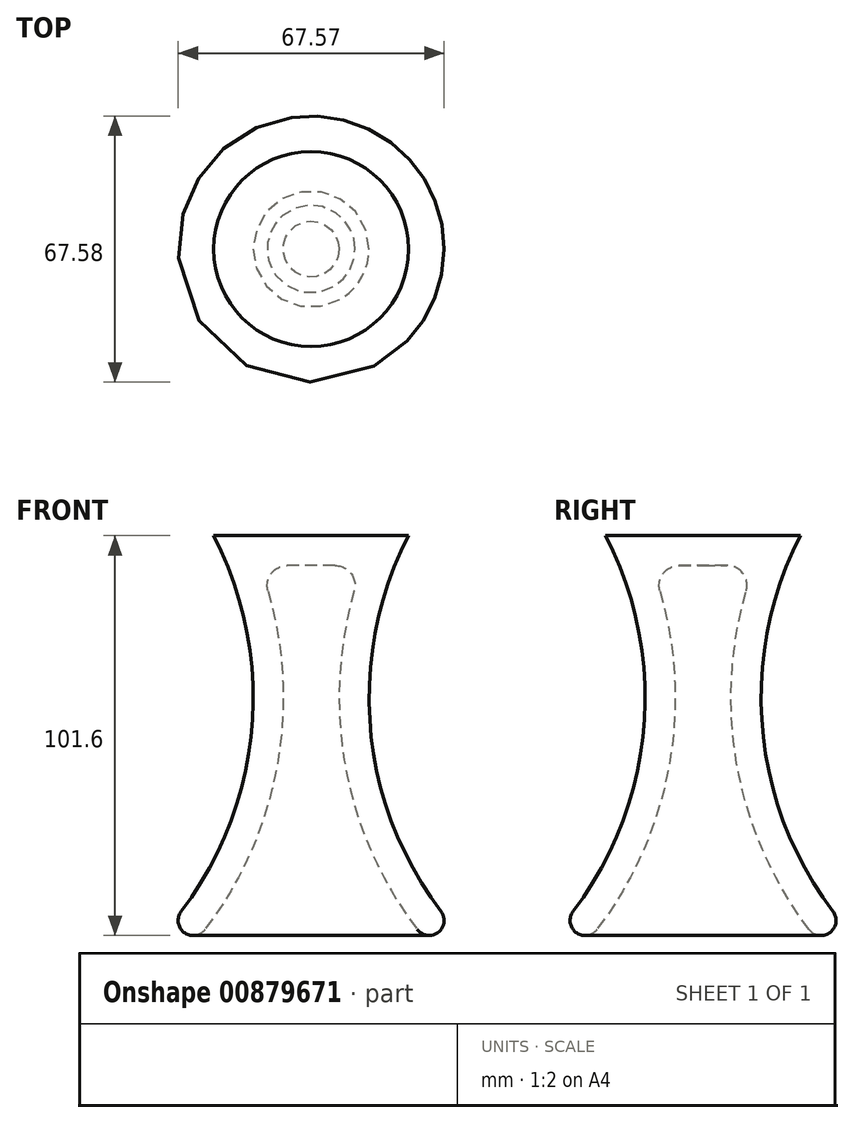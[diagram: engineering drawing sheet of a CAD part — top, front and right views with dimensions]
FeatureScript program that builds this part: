
annotation { "Feature Type Name" : "Feature", "Feature Type Description" : "" }
export const myFeature = defineFeature(function(context is Context, id is Id, definition is map)
    precondition{}
    {
        {
            var Q0;
            Q0=qCreatedBy(makeId("Front.planeOp"),FACE);
            var sketch = newSketch(context, id + "F0", { "sketchPlane" : qUnion([Q0])});
            skLineSegment(sketch, "E0", {"start": v(143.9, 51.31) * mm, "end": v(143.9, -50.29) * mm});
            skLineSegment(sketch, "E1", {"start": v(143.9, 51.31) * mm, "end": v(119.14, 51.31) * mm});
            skLineSegment(sketch, "E2", {"start": v(143.9, -50.29) * mm, "end": v(105.8, -50.29) * mm});
            skArc(sketch, "E3", {"start": v(105.8, -50.29) * mm, "mid": v(128.4, -1.58) * mm, "end": v(119.14, 51.31) * mm});
            skSolve(sketch);
        }
        {
            var Q0;
            Q0=makeQuery(id+"F0.imprint","IMPRINT",FACE,{"disambiguationData":[TD([[makeQuery(id+"F0.imprint","IMPRINT",EDGE,{"derivedFrom":sQuery(id+"F0.wireOp",EDGE,"E0")}),-1.0]])]});
            var Q1;
            Q1=sQuery(id+"F0.wireOp",EDGE,"E0");
            revolve(context, id + "F1", {"surfaceOperationType" : NewSurfaceOperationType.NEW, "entities" : qUnion([Q0]), "axis" : qUnion([Q1]), "revolveType" : RevolveType.FULL});
        }
        {
            var Q0;
            Q0=makeQuery(id+"F1.opRevolve","SWEPT_FACE",FACE,{"disambiguationData":[OSD([sQuery(id+"F0.wireOp",EDGE,"E2")])]});
            shell(context, id + "F2", {"entities" : qUnion([Q0]), "thickness" : 7.62 * mm});
        }
        {
            var Q0;
            Q0=makeQuery(id+"F2.opShell","OFFSET_EDGE",EDGE,{"disambiguationData":[OSD([sQuery(id+"F0.wireOp",EDGE,"E2"),sQuery(id+"F0.wireOp",EDGE,"E3")])]});
            var Q1;
            Q1=makeQuery(id+"F1.opRevolve","SWEPT_EDGE",EDGE,{"disambiguationData":[OSD([sQuery(id+"F0.wireOp",EDGE,"E2"),sQuery(id+"F0.wireOp",EDGE,"E3")])]});
            fillet(context, id + "F3", {"entities" : qUnion([Q0, Q1]), "radius" : 3.8 * mm, "tangentPropagation" : true, "allowEdgeOverflow" : false});
        }
        {
            var Q0;
            Q0=makeQuery(id+"F2.opShell","OFFSET_FACE",FACE,{"disambiguationData":[OSD([sQuery(id+"F0.wireOp",EDGE,"E1")])]});
            fillet(context, id + "F4", {"entities" : qUnion([Q0]), "radius" : 5.08 * mm, "tangentPropagation" : true, "allowEdgeOverflow" : false});
        }
    });
